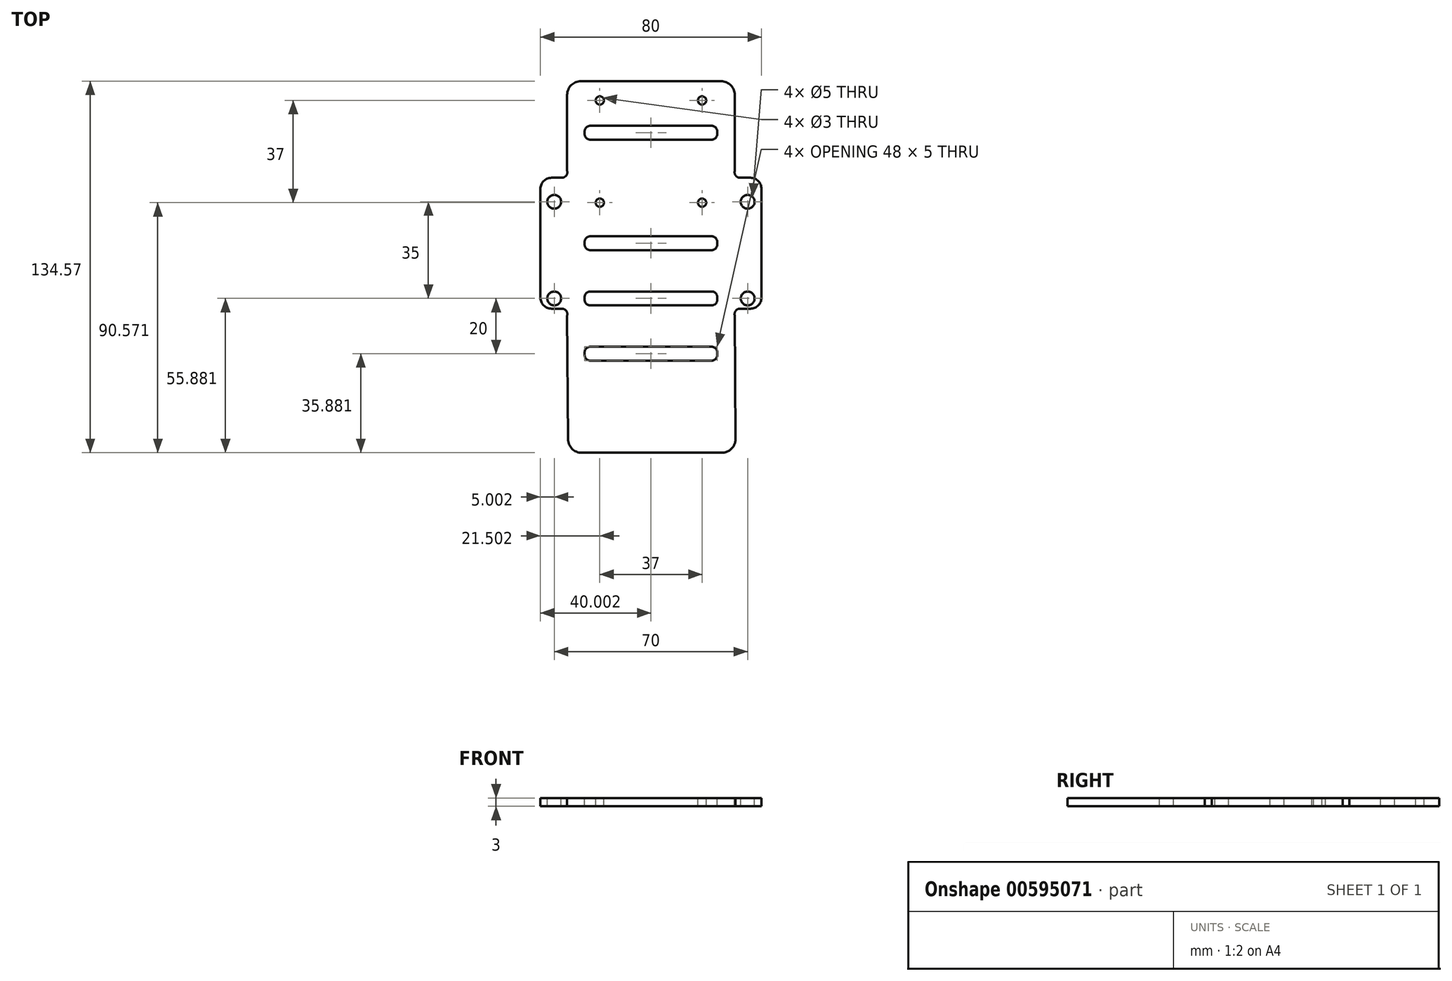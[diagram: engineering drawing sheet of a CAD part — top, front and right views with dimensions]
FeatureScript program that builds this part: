
annotation { "Feature Type Name" : "Feature", "Feature Type Description" : "" }
export const myFeature = defineFeature(function(context is Context, id is Id, definition is map)
    precondition{}
    {
        {
            var Q0;
            Q0=qCreatedBy(makeId("Top.planeOp"),FACE);
            var sketch = newSketch(context, id + "F0", { "sketchPlane" : qUnion([Q0])});
            skLineSegment(sketch, "E0.bottom", {"start": v(2.49, -11.45) * mm, "end": v(-1.26, -11.45) * mm});
            skLineSegment(sketch, "E0.top", {"start": v(2.49, -58.83) * mm, "end": v(-1.26, -58.83) * mm});
            skLineSegment(sketch, "E0.right", {"start": v(-5.26, -15.45) * mm, "end": v(-5.26, -54.83) * mm});
            skLineSegment(sketch, "E1.bottom", {"start": v(67, -58.83) * mm, "end": v(70.74, -58.83) * mm});
            skLineSegment(sketch, "E1.top", {"start": v(67, -11.45) * mm, "end": v(70.74, -11.45) * mm});
            skLineSegment(sketch, "E1.right", {"start": v(74.74, -54.83) * mm, "end": v(74.74, -15.45) * mm});
            skLineSegment(sketch, "E2", {"start": v(-0.26, -11.45) * mm, "end": v(-0.26, -58.83) * mm, "construction": true});
            skLineSegment(sketch, "E3", {"start": v(-0.26, -58.83) * mm, "end": v(-0.28, -58.12) * mm, "construction": true});
            skLineSegment(sketch, "E4", {"start": v(64.74, -20.14) * mm, "end": v(74.74, -20.14) * mm, "construction": true});
            skCircle(sketch, "E5", {"center": v(69.74, -20.14) * mm, "radius": 2.5 * mm});
            skCircle(sketch, "E6", {"center": v(69.74, -55.14) * mm, "radius": 2.5 * mm});
            skArc(sketch, "E7.filletArc", {"start": v(74.74, -15.45) * mm, "mid": v(73.57, -12.62) * mm, "end": v(70.74, -11.45) * mm});
            skArc(sketch, "E8.filletArc", {"start": v(65.06, -8.95) * mm, "mid": v(65.41, -10.67) * mm, "end": v(67, -11.45) * mm});
            skArc(sketch, "E9.filletArc", {"start": v(70.74, -58.83) * mm, "mid": v(73.57, -57.66) * mm, "end": v(74.74, -54.83) * mm});
            skPoint(sketch, "E10.visualSharp", {"position": v(64.74, -58.83) * mm});
            skArc(sketch, "E10.filletArc", {"start": v(67, -58.83) * mm, "mid": v(65.41, -59.6) * mm, "end": v(65.06, -61.33) * mm});
            skPoint(sketch, "E11.visualSharp", {"position": v(-5.26, -11.45) * mm});
            skArc(sketch, "E11.filletArc", {"start": v(-1.26, -11.45) * mm, "mid": v(-4.09, -12.62) * mm, "end": v(-5.26, -15.45) * mm});
            skPoint(sketch, "E12.visualSharp", {"position": v(-5.26, -58.83) * mm});
            skArc(sketch, "E12.filletArc", {"start": v(-5.26, -54.83) * mm, "mid": v(-4.09, -57.66) * mm, "end": v(-1.26, -58.83) * mm});
            skPoint(sketch, "E13.visualSharp", {"position": v(4.74, -58.83) * mm});
            skArc(sketch, "E13.filletArc", {"start": v(4.42, -61.33) * mm, "mid": v(4.07, -59.6) * mm, "end": v(2.49, -58.83) * mm});
            skArc(sketch, "E14.filletArc", {"start": v(2.49, -11.45) * mm, "mid": v(4.07, -10.67) * mm, "end": v(4.42, -8.95) * mm});
            skCircle(sketch, "E15.MirrorC", {"center": v(-0.26, -20.14) * mm, "radius": 2.5 * mm});
            skCircle(sketch, "E16.MirrorC", {"center": v(-0.26, -55.14) * mm, "radius": 2.5 * mm});
            skPoint(sketch, "E17.middle", {"position": v(34.74, -15.14) * mm});
            skLineSegment(sketch, "E18.MirrorCS", {"start": v(12.74, -57.64) * mm, "end": v(56.74, -57.64) * mm});
            skLineSegment(sketch, "E19.MirrorCS", {"start": v(12.74, -52.64) * mm, "end": v(56.74, -52.64) * mm});
            skLineSegment(sketch, "E20.MirrorCS", {"start": v(58.74, -54.64) * mm, "end": v(58.74, -55.64) * mm});
            skLineSegment(sketch, "E21.MirrorCS", {"start": v(10.74, -54.64) * mm, "end": v(10.74, -55.64) * mm});
            skLineSegment(sketch, "E22.bottom", {"start": v(56.74, -32.64) * mm, "end": v(12.74, -32.64) * mm});
            skLineSegment(sketch, "E22.top", {"start": v(56.74, -37.64) * mm, "end": v(12.74, -37.64) * mm});
            skLineSegment(sketch, "E22.left", {"start": v(58.74, -34.64) * mm, "end": v(58.74, -35.64) * mm});
            skLineSegment(sketch, "E22.right", {"start": v(10.74, -34.64) * mm, "end": v(10.74, -35.64) * mm});
            skPoint(sketch, "E22.middle", {"position": v(34.74, -35.14) * mm});
            skPoint(sketch, "E23.MirrorCS.start.orphan", {"position": v(-1.26, -27.12) * mm});
            skLineSegment(sketch, "E24.bottom", {"start": v(12.74, -72.64) * mm, "end": v(56.74, -72.64) * mm});
            skLineSegment(sketch, "E24.top", {"start": v(12.74, -77.64) * mm, "end": v(56.74, -77.64) * mm});
            skLineSegment(sketch, "E24.left", {"start": v(10.74, -74.64) * mm, "end": v(10.74, -75.64) * mm});
            skLineSegment(sketch, "E24.right", {"start": v(58.74, -74.64) * mm, "end": v(58.74, -75.64) * mm});
            skPoint(sketch, "E24.middle", {"position": v(34.74, -75.14) * mm});
            skLineSegment(sketch, "E25.bottom", {"start": v(12.74, 2.36) * mm, "end": v(56.74, 2.36) * mm});
            skLineSegment(sketch, "E25.top", {"start": v(12.74, 7.36) * mm, "end": v(56.74, 7.36) * mm});
            skLineSegment(sketch, "E25.left", {"start": v(10.74, 4.36) * mm, "end": v(10.74, 5.36) * mm});
            skLineSegment(sketch, "E25.right", {"start": v(58.74, 4.36) * mm, "end": v(58.74, 5.36) * mm});
            skPoint(sketch, "E26.visualSharp", {"position": v(10.74, -77.64) * mm});
            skArc(sketch, "E26.filletArc", {"start": v(10.74, -75.64) * mm, "mid": v(11.33, -77.05) * mm, "end": v(12.74, -77.64) * mm});
            skPoint(sketch, "E27.visualSharp", {"position": v(10.74, -72.64) * mm});
            skArc(sketch, "E27.filletArc", {"start": v(12.74, -72.64) * mm, "mid": v(11.33, -73.22) * mm, "end": v(10.74, -74.64) * mm});
            skPoint(sketch, "E28.visualSharp", {"position": v(58.74, -72.64) * mm});
            skArc(sketch, "E28.filletArc", {"start": v(58.74, -74.64) * mm, "mid": v(58.16, -73.22) * mm, "end": v(56.74, -72.64) * mm});
            skPoint(sketch, "E29.visualSharp", {"position": v(58.74, -77.64) * mm});
            skArc(sketch, "E29.filletArc", {"start": v(56.74, -77.64) * mm, "mid": v(58.16, -77.05) * mm, "end": v(58.74, -75.64) * mm});
            skPoint(sketch, "E30.visualSharp", {"position": v(58.74, -52.64) * mm});
            skArc(sketch, "E30.filletArc", {"start": v(58.74, -54.64) * mm, "mid": v(58.16, -53.22) * mm, "end": v(56.74, -52.64) * mm});
            skPoint(sketch, "E31.visualSharp", {"position": v(10.74, -52.64) * mm});
            skArc(sketch, "E31.filletArc", {"start": v(12.74, -52.64) * mm, "mid": v(11.33, -53.22) * mm, "end": v(10.74, -54.64) * mm});
            skPoint(sketch, "E32.visualSharp", {"position": v(10.74, -57.64) * mm});
            skArc(sketch, "E32.filletArc", {"start": v(10.74, -55.64) * mm, "mid": v(11.33, -57.05) * mm, "end": v(12.74, -57.64) * mm});
            skPoint(sketch, "E33.visualSharp", {"position": v(58.74, -57.64) * mm});
            skArc(sketch, "E33.filletArc", {"start": v(56.74, -57.64) * mm, "mid": v(58.16, -57.05) * mm, "end": v(58.74, -55.64) * mm});
            skPoint(sketch, "E34.visualSharp", {"position": v(10.74, -37.64) * mm});
            skArc(sketch, "E34.filletArc", {"start": v(10.74, -35.64) * mm, "mid": v(11.33, -37.05) * mm, "end": v(12.74, -37.64) * mm});
            skPoint(sketch, "E35.visualSharp", {"position": v(10.74, -32.64) * mm});
            skArc(sketch, "E35.filletArc", {"start": v(12.74, -32.64) * mm, "mid": v(11.33, -33.22) * mm, "end": v(10.74, -34.64) * mm});
            skPoint(sketch, "E36.visualSharp", {"position": v(58.74, -32.64) * mm});
            skArc(sketch, "E36.filletArc", {"start": v(58.74, -34.64) * mm, "mid": v(58.16, -33.22) * mm, "end": v(56.74, -32.64) * mm});
            skPoint(sketch, "E37.visualSharp", {"position": v(58.74, -37.64) * mm});
            skArc(sketch, "E37.filletArc", {"start": v(56.74, -37.64) * mm, "mid": v(58.16, -37.05) * mm, "end": v(58.74, -35.64) * mm});
            skPoint(sketch, "E38.visualSharp", {"position": v(10.74, -17.64) * mm});
            skArc(sketch, "E39.filletArc", {"start": v(10.74, 4.36) * mm, "mid": v(11.33, 2.95) * mm, "end": v(12.74, 2.36) * mm});
            skArc(sketch, "E40.filletArc", {"start": v(12.74, 7.36) * mm, "mid": v(11.33, 6.78) * mm, "end": v(10.74, 5.36) * mm});
            skArc(sketch, "E41.filletArc", {"start": v(58.74, 5.36) * mm, "mid": v(58.16, 6.78) * mm, "end": v(56.74, 7.36) * mm});
            skArc(sketch, "E42.filletArc", {"start": v(56.74, 2.36) * mm, "mid": v(58.16, 2.95) * mm, "end": v(58.74, 4.36) * mm});
            skLineSegment(sketch, "E43.trimOffspring", {"start": v(4.74, -55.14) * mm, "end": v(4.74, -58.83) * mm});
            skLineSegment(sketch, "E44", {"start": v(9.42, 23.55) * mm, "end": v(60.06, 23.55) * mm});
            skLineSegment(sketch, "E45", {"start": v(65.06, -8.95) * mm, "end": v(65.06, 18.55) * mm});
            skPoint(sketch, "E46.visualSharp", {"position": v(65.06, 23.55) * mm});
            skArc(sketch, "E46.filletArc", {"start": v(65.06, 18.55) * mm, "mid": v(63.6, 22.09) * mm, "end": v(60.06, 23.55) * mm});
            skLineSegment(sketch, "E47", {"start": v(4.42, -8.95) * mm, "end": v(4.42, 18.55) * mm});
            skPoint(sketch, "E48.visualSharp", {"position": v(4.42, 23.55) * mm});
            skArc(sketch, "E48.filletArc", {"start": v(9.42, 23.55) * mm, "mid": v(5.89, 22.09) * mm, "end": v(4.42, 18.55) * mm});
            skLineSegment(sketch, "E49", {"start": v(4.42, -61.33) * mm, "end": v(4.7, -106.05) * mm});
            skLineSegment(sketch, "E50", {"start": v(65.06, -61.33) * mm, "end": v(65.34, -105.99) * mm});
            skLineSegment(sketch, "E51", {"start": v(9.7, -111.02) * mm, "end": v(60.34, -111.02) * mm});
            skPoint(sketch, "E52.visualSharp", {"position": v(4.74, -111.02) * mm});
            skArc(sketch, "E52.filletArc", {"start": v(4.7, -106.05) * mm, "mid": v(6.19, -109.56) * mm, "end": v(9.7, -111.02) * mm});
            skPoint(sketch, "E53.visualSharp", {"position": v(65.38, -111.02) * mm});
            skArc(sketch, "E53.filletArc", {"start": v(60.34, -111.02) * mm, "mid": v(63.9, -109.54) * mm, "end": v(65.34, -105.99) * mm});
            skLineSegment(sketch, "E54", {"start": v(34.74, 23.55) * mm, "end": v(34.74, -111.02) * mm, "construction": true});
            skLineSegment(sketch, "E55", {"start": v(4.42, 16.55) * mm, "end": v(65.06, 16.55) * mm, "construction": true});
            skLineSegment(sketch, "E56", {"start": v(4.42, -20.45) * mm, "end": v(65.06, -20.45) * mm, "construction": true});
            skLineSegment(sketch, "E57", {"start": v(16.24, 16.55) * mm, "end": v(16.24, -20.45) * mm, "construction": true});
            skLineSegment(sketch, "E58", {"start": v(53.24, 16.55) * mm, "end": v(53.24, -20.45) * mm, "construction": true});
            skCircle(sketch, "E59", {"center": v(16.24, -20.45) * mm, "radius": 1.5 * mm});
            skCircle(sketch, "E60", {"center": v(53.24, -20.45) * mm, "radius": 1.5 * mm});
            skCircle(sketch, "E61", {"center": v(53.24, 16.55) * mm, "radius": 1.5 * mm});
            skCircle(sketch, "E62", {"center": v(16.24, 16.55) * mm, "radius": 1.5 * mm});
            skSolve(sketch);
        }
        {
            var Q0;
            Q0 = qSketchRegion(id + "F0", true);
            extrude(context, id + "F1", {"entities" : qUnion([Q0]), "oppositeDirection" : true, "depth" : 3 * mm, "offsetDistance" : 25 * mm});
        }
    });
